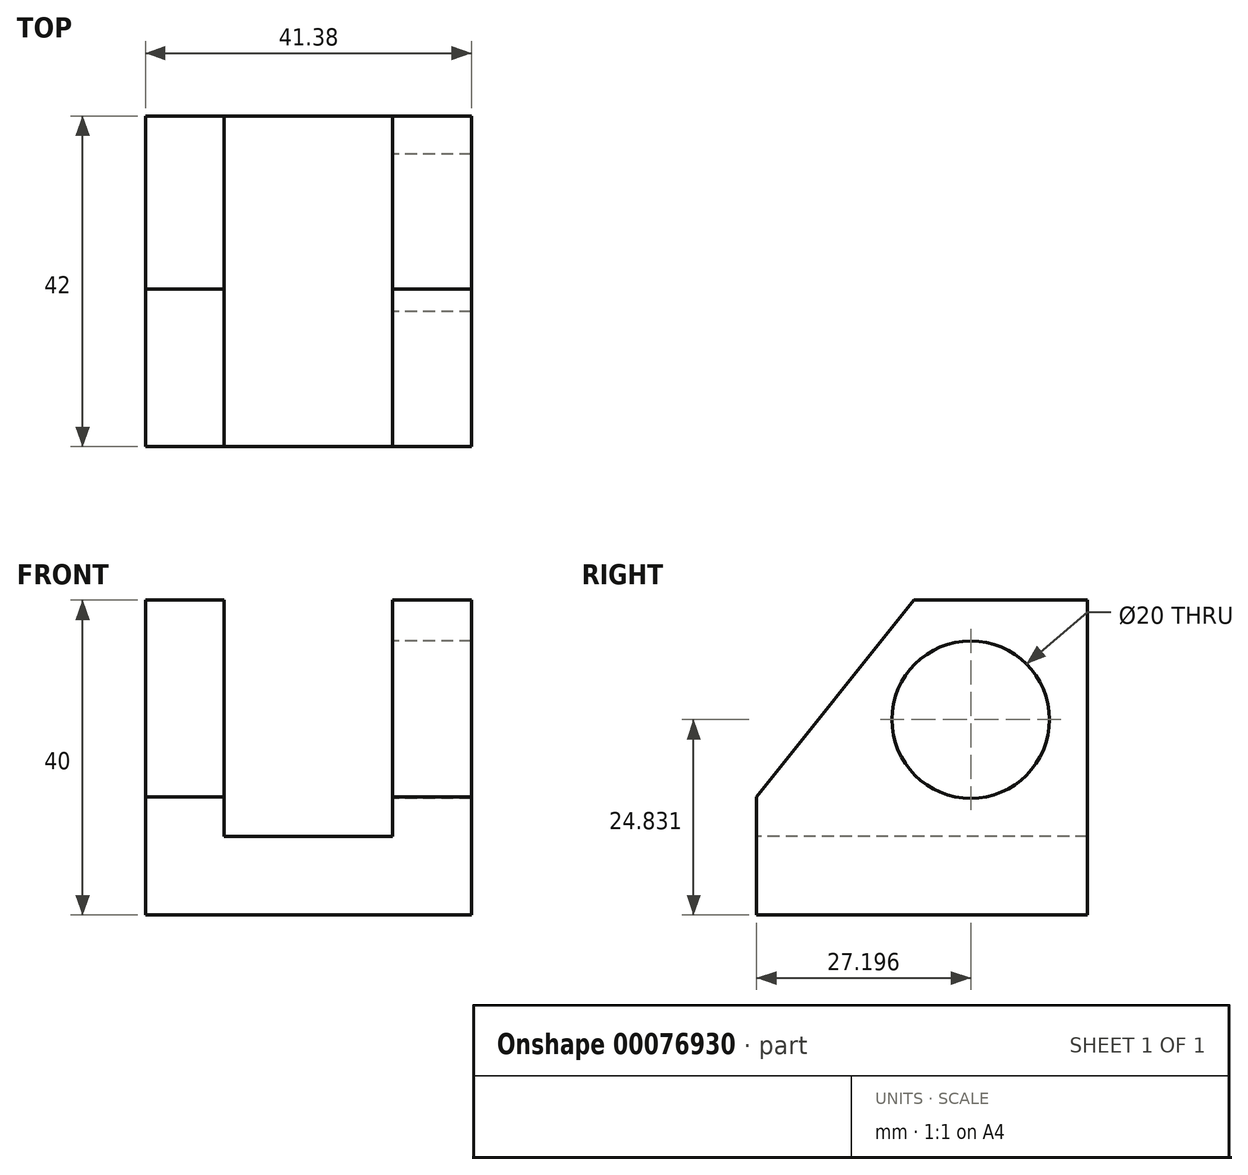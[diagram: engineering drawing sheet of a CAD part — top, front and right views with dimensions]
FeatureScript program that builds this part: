
annotation { "Feature Type Name" : "Feature", "Feature Type Description" : "" }
export const myFeature = defineFeature(function(context is Context, id is Id, definition is map)
    precondition{}
    {
        {
            var Q0;
            Q0=qCreatedBy(makeId("Front.planeOp"),FACE);
            var sketch = newSketch(context, id + "F0", { "sketchPlane" : qUnion([Q0])});
            skLineSegment(sketch, "E0", {"start": v(-20.69, 0) * mm, "end": v(-20.69, 40) * mm});
            skLineSegment(sketch, "E1", {"start": v(-20.69, 40) * mm, "end": v(-10.69, 40) * mm});
            skLineSegment(sketch, "E2", {"start": v(-10.69, 40) * mm, "end": v(-10.69, 10) * mm});
            skLineSegment(sketch, "E3.MirrorCS", {"start": v(20.69, 0) * mm, "end": v(20.69, 40) * mm});
            skLineSegment(sketch, "E4.MirrorCS", {"start": v(10.69, 40) * mm, "end": v(10.69, 10) * mm});
            skLineSegment(sketch, "E5.MirrorCS", {"start": v(20.69, 40) * mm, "end": v(10.69, 40) * mm});
            skLineSegment(sketch, "E6", {"start": v(-20.69, 0) * mm, "end": v(20.69, 0) * mm});
            skLineSegment(sketch, "E7", {"start": v(-10.69, 10) * mm, "end": v(10.69, 10) * mm});
            skSolve(sketch);
        }
        {
            var Q0;
            Q0=makeQuery(id+"F0.imprint","IMPRINT",FACE,{"disambiguationData":[TD([[makeQuery(id+"F0.imprint","IMPRINT",EDGE,{"derivedFrom":sQuery(id+"F0.wireOp",EDGE,"E0")}),-1.0]])]});
            extrude(context, id + "F1", {"entities" : qUnion([Q0]), "oppositeDirection" : true, "depth" : 42 * mm});
        }
        {
            var Q0;
            Q0=qCreatedBy(makeId("Right.planeOp"),FACE);
            var sketch = newSketch(context, id + "F2", { "sketchPlane" : qUnion([Q0])});
            skPoint(sketch, "E8", {"position": v(27.2, 24.83) * mm});
            skSolve(sketch);
        }
        {
            var Q0;
            Q0=makeQuery(id+"F1.opExtrude","CAP_EDGE",EDGE,{"disambiguationData":[OSD([sQuery(id+"F0.wireOp",EDGE,"E1")])],"isStart":true});
            var Q1;
            Q1=makeQuery(id+"F1.opExtrude","CAP_EDGE",EDGE,{"disambiguationData":[OSD([sQuery(id+"F0.wireOp",EDGE,"E5.MirrorCS")])],"isStart":true});
            chamfer(context, id + "F3", {"entities" : qUnion([Q0, Q1]), "chamferType" : ChamferType.TWO_OFFSETS, "width1" : 20 * mm, "oppositeDirection" : false, "width2" : 25 * mm, "tangentPropagation" : true});
        }
        {
            var Q0;
            Q0=sQuery(id+"F2.wireOp",VERTEX,"E8");
            var Q1;
            Q1=makeQuery(id+"F1.opExtrude","SWEPT_BODY",BODY,{"disambiguationData":[OSD([sQuery(id+"F0.wireOp",EDGE,"E0"),sQuery(id+"F0.wireOp",EDGE,"E1"),sQuery(id+"F0.wireOp",EDGE,"E2"),sQuery(id+"F0.wireOp",EDGE,"E3.MirrorCS"),sQuery(id+"F0.wireOp",EDGE,"E4.MirrorCS"),sQuery(id+"F0.wireOp",EDGE,"E5.MirrorCS"),sQuery(id+"F0.wireOp",EDGE,"E6"),sQuery(id+"F0.wireOp",EDGE,"E7")])]});
            hole(context, id + "F4", {"style" : HoleStyle.SIMPLE, "endStyle" : HoleEndStyle.THROUGH, "oppositeDirection" : true, "holeDiameter" : 20 * mm, "locations" : qUnion([Q0]), "scope" : qUnion([Q1]), "isTappedThrough" : true});
        }
    });
